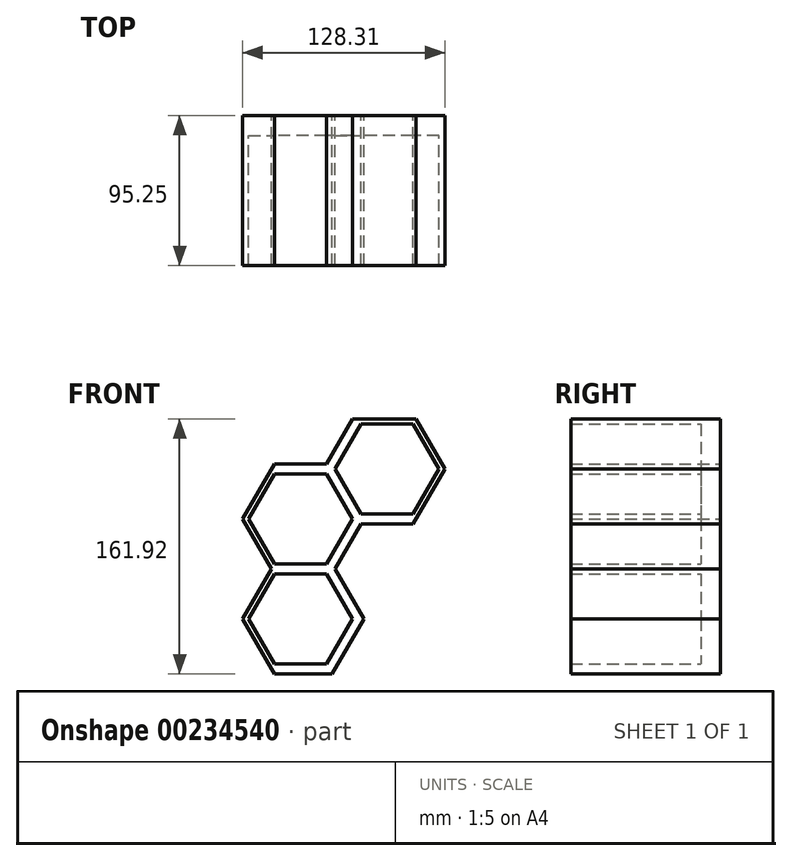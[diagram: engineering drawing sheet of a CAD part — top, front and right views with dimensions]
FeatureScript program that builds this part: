
annotation { "Feature Type Name" : "Feature", "Feature Type Description" : "" }
export const myFeature = defineFeature(function(context is Context, id is Id, definition is map)
    precondition{}
    {
        {
            var Q0;
            Q0=qCreatedBy(makeId("Front.planeOp"),FACE);
            var sketch = newSketch(context, id + "F0", { "sketchPlane" : qUnion([Q0])});
            skLineSegment(sketch, "E0.1", {"start": v(-4.28, 35.04) * mm, "end": v(27.5, 35.04) * mm});
            skCircle(sketch, "E1.cCircle", {"center": v(-40.94, 35.04) * mm, "radius": 28.58 * mm, "construction": true});
            skLineSegment(sketch, "E1.0", {"start": v(-73.94, 35.04) * mm, "end": v(-57.44, 63.62) * mm});
            skLineSegment(sketch, "E1.1", {"start": v(-57.44, 63.62) * mm, "end": v(-24.44, 63.62) * mm});
            skLineSegment(sketch, "E1.2", {"start": v(-24.44, 63.62) * mm, "end": v(-7.94, 35.04) * mm});
            skLineSegment(sketch, "E1.3", {"start": v(-7.94, 35.04) * mm, "end": v(-24.44, 6.47) * mm});
            skLineSegment(sketch, "E1.4", {"start": v(-24.44, 6.47) * mm, "end": v(-57.44, 6.47) * mm});
            skLineSegment(sketch, "E1.5", {"start": v(-57.44, 6.47) * mm, "end": v(-73.94, 35.04) * mm});
            skPoint(sketch, "E1.0.midPoint", {"position": v(-65.69, 49.33) * mm});
            skCircle(sketch, "E2.cCircle", {"center": v(-40.94, 35.04) * mm, "radius": 31.75 * mm, "construction": true});
            skLineSegment(sketch, "E2.0", {"start": v(-77.6, 35.04) * mm, "end": v(-59.27, 66.8) * mm});
            skLineSegment(sketch, "E2.1", {"start": v(-59.27, 66.8) * mm, "end": v(-22.6, 66.8) * mm});
            skLineSegment(sketch, "E2.2", {"start": v(-22.6, 66.8) * mm, "end": v(-4.28, 35.04) * mm});
            skLineSegment(sketch, "E2.3", {"start": v(-4.28, 35.04) * mm, "end": v(-22.6, 3.3) * mm});
            skLineSegment(sketch, "E2.4", {"start": v(-22.6, 3.3) * mm, "end": v(-59.27, 3.3) * mm});
            skLineSegment(sketch, "E2.5", {"start": v(-59.27, 3.3) * mm, "end": v(-77.6, 35.04) * mm});
            skPoint(sketch, "E2.0.midPoint", {"position": v(-68.44, 50.92) * mm});
            skLineSegment(sketch, "E3.2", {"start": v(-77.6, 35.04) * mm, "end": v(-59.27, 3.3) * mm});
            skLineSegment(sketch, "E3.3", {"start": v(-59.27, 3.3) * mm, "end": v(-77.6, -28.46) * mm});
            skLineSegment(sketch, "E4.3", {"start": v(-59.27, 66.8) * mm, "end": v(-77.6, 35.04) * mm});
            skCircle(sketch, "E5.cCircle", {"center": v(14.05, 66.8) * mm, "radius": 28.58 * mm, "construction": true});
            skLineSegment(sketch, "E5.0", {"start": v(-18.94, 66.8) * mm, "end": v(-2.45, 95.37) * mm});
            skLineSegment(sketch, "E5.1", {"start": v(-2.45, 95.37) * mm, "end": v(30.55, 95.37) * mm});
            skLineSegment(sketch, "E5.2", {"start": v(30.55, 95.37) * mm, "end": v(47.05, 66.8) * mm});
            skLineSegment(sketch, "E5.3", {"start": v(47.05, 66.8) * mm, "end": v(30.55, 38.22) * mm});
            skLineSegment(sketch, "E5.4", {"start": v(30.55, 38.22) * mm, "end": v(-2.45, 38.22) * mm});
            skLineSegment(sketch, "E5.5", {"start": v(-2.45, 38.22) * mm, "end": v(-18.94, 66.8) * mm});
            skPoint(sketch, "E5.0.midPoint", {"position": v(-10.7, 81.08) * mm});
            skCircle(sketch, "E6.cCircle", {"center": v(14.05, 66.8) * mm, "radius": 31.75 * mm, "construction": true});
            skLineSegment(sketch, "E6.0", {"start": v(-22.6, 66.8) * mm, "end": v(-4.28, 98.54) * mm});
            skLineSegment(sketch, "E6.1", {"start": v(-4.28, 98.54) * mm, "end": v(32.38, 98.54) * mm});
            skLineSegment(sketch, "E6.2", {"start": v(32.38, 98.54) * mm, "end": v(50.71, 66.8) * mm});
            skLineSegment(sketch, "E6.3", {"start": v(50.71, 66.8) * mm, "end": v(32.38, 35.04) * mm});
            skLineSegment(sketch, "E6.4", {"start": v(32.38, 35.04) * mm, "end": v(-4.28, 35.04) * mm});
            skLineSegment(sketch, "E6.5", {"start": v(-4.28, 35.04) * mm, "end": v(-22.6, 66.8) * mm});
            skPoint(sketch, "E6.0.midPoint", {"position": v(-13.44, 82.67) * mm});
            skLineSegment(sketch, "E7.4", {"start": v(-27.5, 66.8) * mm, "end": v(-59.27, 66.8) * mm});
            skCircle(sketch, "E8.cCircle", {"center": v(-40.94, -28.46) * mm, "radius": 28.58 * mm, "construction": true});
            skLineSegment(sketch, "E8.0", {"start": v(-73.94, -28.46) * mm, "end": v(-57.44, 0.12) * mm});
            skLineSegment(sketch, "E8.1", {"start": v(-57.44, 0.12) * mm, "end": v(-24.44, 0.12) * mm});
            skLineSegment(sketch, "E8.2", {"start": v(-24.44, 0.12) * mm, "end": v(-7.94, -28.46) * mm});
            skLineSegment(sketch, "E8.3", {"start": v(-7.94, -28.46) * mm, "end": v(-24.44, -57.03) * mm});
            skLineSegment(sketch, "E8.4", {"start": v(-24.44, -57.03) * mm, "end": v(-57.44, -57.03) * mm});
            skLineSegment(sketch, "E8.5", {"start": v(-57.44, -57.03) * mm, "end": v(-73.94, -28.46) * mm});
            skPoint(sketch, "E8.0.midPoint", {"position": v(-65.69, -14.17) * mm});
            skCircle(sketch, "E9.cCircle", {"center": v(-40.94, -28.46) * mm, "radius": 31.75 * mm, "construction": true});
            skLineSegment(sketch, "E9.0", {"start": v(-77.6, -28.46) * mm, "end": v(-59.27, 3.3) * mm});
            skLineSegment(sketch, "E9.1", {"start": v(-59.27, 3.3) * mm, "end": v(-22.6, 3.3) * mm});
            skLineSegment(sketch, "E9.2", {"start": v(-22.6, 3.3) * mm, "end": v(-4.28, -28.46) * mm});
            skLineSegment(sketch, "E9.3", {"start": v(-4.28, -28.46) * mm, "end": v(-22.6, -60.2) * mm});
            skLineSegment(sketch, "E9.4", {"start": v(-22.6, -60.2) * mm, "end": v(-59.27, -60.2) * mm});
            skLineSegment(sketch, "E9.5", {"start": v(-59.27, -60.2) * mm, "end": v(-77.6, -28.46) * mm});
            skPoint(sketch, "E9.0.midPoint", {"position": v(-68.44, -12.58) * mm});
            skLineSegment(sketch, "E10.2", {"start": v(-77.6, -28.46) * mm, "end": v(-59.27, -60.2) * mm});
            skLineSegment(sketch, "E11.4", {"start": v(32.38, 98.54) * mm, "end": v(-4.28, 98.54) * mm});
            skLineSegment(sketch, "E12.5", {"start": v(50.71, 66.8) * mm, "end": v(32.38, 98.54) * mm});
            skLineSegment(sketch, "E13.0", {"start": v(32.38, 35.04) * mm, "end": v(50.71, 66.8) * mm});
            skPoint(sketch, "E13.0.midPoint", {"position": v(41.55, 50.92) * mm});
            skLineSegment(sketch, "E14", {"start": v(-57.44, -63.38) * mm, "end": v(-20.78, -63.38) * mm});
            skLineSegment(sketch, "E15", {"start": v(-20.78, -63.38) * mm, "end": v(-0.61, -28.46) * mm});
            skLineSegment(sketch, "E16", {"start": v(-0.61, -28.46) * mm, "end": v(-18.94, 3.3) * mm});
            skLineSegment(sketch, "E17", {"start": v(-18.94, 3.3) * mm, "end": v(-2.45, 31.87) * mm});
            skLineSegment(sketch, "E18", {"start": v(-2.45, 31.87) * mm, "end": v(30.55, 31.87) * mm});
            skLineSegment(sketch, "E19", {"start": v(-57.44, 69.97) * mm, "end": v(-24.44, 69.97) * mm});
            skLineSegment(sketch, "E20", {"start": v(-24.44, 69.97) * mm, "end": v(-7.94, 98.54) * mm});
            skLineSegment(sketch, "E21", {"start": v(-7.94, 98.54) * mm, "end": v(-4.28, 98.54) * mm});
            skLineSegment(sketch, "E22", {"start": v(-57.44, 69.97) * mm, "end": v(-59.27, 66.8) * mm});
            skLineSegment(sketch, "E23", {"start": v(-59.27, -60.2) * mm, "end": v(-57.44, -63.38) * mm});
            skLineSegment(sketch, "E24", {"start": v(30.55, 31.87) * mm, "end": v(32.38, 35.04) * mm});
            skSolve(sketch);
        }
        {
            var Q0;
            Q0=makeQuery(id+"F0.imprint","IMPRINT",FACE,{"disambiguationData":[TD([[makeQuery(id+"F0.imprint","IMPRINT",EDGE,{"derivedFrom":sQuery(id+"F0.wireOp",EDGE,"68d16a58-0471-4e1c-b2b3-2a61df7c0d9d.0")}),-1.0]])]});
            var Q1;
            Q1=makeQuery(id+"F0.imprint","IMPRINT",FACE,{"disambiguationData":[TD([[makeQuery(id+"F0.imprint","IMPRINT",EDGE,{"derivedFrom":sQuery(id+"F0.wireOp",EDGE,"ae29455d-c252-400a-b569-c5a1c48e1351.0")}),-1.0]])]});
            var Q2;
            Q2=makeQuery(id+"F0.imprint","IMPRINT",FACE,{"disambiguationData":[TD([[makeQuery(id+"F0.imprint","IMPRINT",EDGE,{"derivedFrom":sQuery(id+"F0.wireOp",EDGE,"cad1e4f3-bd43-45ec-b31a-1d5006939c94.0")}),-1.0]])]});
            var Q3;
            Q3=makeQuery(id+"F0.imprint","IMPRINT",FACE,{"disambiguationData":[TD([[makeQuery(id+"F0.imprint","IMPRINT",EDGE,{"derivedFrom":sQuery(id+"F0.wireOp",EDGE,"b43d4d8c-f78a-4ff8-8565-99a66ce6ec5f.0")}),-1.0]])]});
            var Q4;
            Q4=makeQuery(id+"F0.imprint","IMPRINT",FACE,{"disambiguationData":[TD([[makeQuery(id+"F0.imprint","IMPRINT",EDGE,{"derivedFrom":sQuery(id+"F0.wireOp",EDGE,"8c75d941-d110-4871-aa41-90a72d60fb2b.0")}),-1.0]])]});
            var Q5;
            Q5=makeQuery(id+"F0.imprint","IMPRINT",FACE,{"disambiguationData":[TD([[makeQuery(id+"F0.imprint","IMPRINT",EDGE,{"derivedFrom":sQuery(id+"F0.wireOp",EDGE,"258573fa-3544-418e-8bc5-5d37e5b8ba09.0")}),-1.0]])]});
            var Q6;
            Q6=makeQuery(id+"F0.imprint","IMPRINT",FACE,{"disambiguationData":[TD([[makeQuery(id+"F0.imprint","IMPRINT",EDGE,{"derivedFrom":sQuery(id+"F0.wireOp",EDGE,"0bf0733b-7d93-4c2e-8366-56d2cde24658.0")}),-1.0]])]});
            var Q7;
            Q7=makeQuery(id+"F0.imprint","IMPRINT",FACE,{"disambiguationData":[TD([[makeQuery(id+"F0.imprint","IMPRINT",EDGE,{"derivedFrom":sQuery(id+"F0.wireOp",EDGE,"E5.0")}),-1.0]])]});
            var Q8;
            Q8=makeQuery(id+"F0.imprint","IMPRINT",FACE,{"disambiguationData":[TD([[makeQuery(id+"F0.imprint","IMPRINT",EDGE,{"derivedFrom":sQuery(id+"F0.wireOp",EDGE,"f16ea8c9-6b67-4651-8441-f7eb3c0ce7d7.0")}),-1.0]])]});
            var Q9;
            Q9=makeQuery(id+"F0.imprint","IMPRINT",FACE,{"disambiguationData":[TD([[makeQuery(id+"F0.imprint","IMPRINT",EDGE,{"derivedFrom":sQuery(id+"F0.wireOp",EDGE,"0306a0a6-7289-4661-a415-5fa5585f2cb5.0")}),-1.0]])]});
            var Q10;
            Q10=makeQuery(id+"F0.imprint","IMPRINT",FACE,{"disambiguationData":[TD([[makeQuery(id+"F0.imprint","IMPRINT",EDGE,{"derivedFrom":sQuery(id+"F0.wireOp",EDGE,"E8.0")}),-1.0]])]});
            var Q11;
            Q11=makeQuery(id+"F0.imprint","IMPRINT",FACE,{"disambiguationData":[TD([[makeQuery(id+"F0.imprint","IMPRINT",EDGE,{"derivedFrom":sQuery(id+"F0.wireOp",EDGE,"cbfd9497-f7fe-4f18-9288-d90aa8075d81.0")}),-1.0]])]});
            var Q12;
            Q12=makeQuery(id+"F0.imprint","IMPRINT",FACE,{"disambiguationData":[TD([[makeQuery(id+"F0.imprint","IMPRINT",EDGE,{"derivedFrom":sQuery(id+"F0.wireOp",EDGE,"6282d196-dd8f-4bb0-bca4-b9108e277473.0")}),-1.0]])]});
            var Q13;
            Q13=makeQuery(id+"F0.imprint","IMPRINT",FACE,{"disambiguationData":[TD([[makeQuery(id+"F0.imprint","IMPRINT",EDGE,{"derivedFrom":sQuery(id+"F0.wireOp",EDGE,"084ca30c-4dc0-463f-bfd9-557787ed9a2f.0")}),-1.0]])]});
            var Q14;
            Q14=makeQuery(id+"F0.imprint","IMPRINT",FACE,{"disambiguationData":[TD([[makeQuery(id+"F0.imprint","IMPRINT",EDGE,{"derivedFrom":sQuery(id+"F0.wireOp",EDGE,"06c29831-6b25-410b-9247-4ee044b7735c.0")}),-1.0]])]});
            var Q15;
            Q15=makeQuery(id+"F0.imprint","IMPRINT",FACE,{"disambiguationData":[TD([[makeQuery(id+"F0.imprint","IMPRINT",EDGE,{"derivedFrom":sQuery(id+"F0.wireOp",EDGE,"b8eec94e-d97e-439b-aaac-63499233db4c.0")}),-1.0]])]});
            var Q16;
            Q16=makeQuery(id+"F0.imprint","IMPRINT",FACE,{"disambiguationData":[TD([[makeQuery(id+"F0.imprint","IMPRINT",EDGE,{"derivedFrom":sQuery(id+"F0.wireOp",EDGE,"2e929887-9bb9-4083-9cef-f9a6a24e8e46.0")}),-1.0]])]});
            var Q17;
            Q17=makeQuery(id+"F0.imprint","IMPRINT",FACE,{"disambiguationData":[TD([[makeQuery(id+"F0.imprint","IMPRINT",EDGE,{"derivedFrom":sQuery(id+"F0.wireOp",EDGE,"23671680-92ab-419e-a071-eb0943a5012b.0")}),-1.0]])]});
            var Q18;
            Q18=makeQuery(id+"F0.imprint","IMPRINT",FACE,{"disambiguationData":[TD([[makeQuery(id+"F0.imprint","IMPRINT",EDGE,{"derivedFrom":sQuery(id+"F0.wireOp",EDGE,"E1.0")}),-1.0]])]});
            var Q19;
            Q19=makeQuery(id+"F0.imprint","IMPRINT",FACE,{"disambiguationData":[TD([[makeQuery(id+"F0.imprint","IMPRINT",EDGE,{"derivedFrom":sQuery(id+"F0.wireOp",EDGE,"37efd634-c264-4683-8864-08b38c7986ca.0")}),-1.0]])]});
            var Q20;
            Q20=makeQuery(id+"F0.imprint","IMPRINT",FACE,{"disambiguationData":[TD([[makeQuery(id+"F0.imprint","IMPRINT",EDGE,{"derivedFrom":sQuery(id+"F0.wireOp",EDGE,"f2dd3995-374a-43c5-8725-4a87181dc8c5.0")}),-1.0]])]});
            var Q21;
            Q21=makeQuery(id+"F0.imprint","IMPRINT",FACE,{"disambiguationData":[TD([[makeQuery(id+"F0.imprint","IMPRINT",EDGE,{"derivedFrom":sQuery(id+"F0.wireOp",EDGE,"1f2aec04-a318-49b9-a42e-ea2fce35ed6c.0")}),-1.0]])]});
            var Q22;
            Q22=makeQuery(id+"F0.imprint","IMPRINT",FACE,{"disambiguationData":[TD([[makeQuery(id+"F0.imprint","IMPRINT",EDGE,{"derivedFrom":sQuery(id+"F0.wireOp",EDGE,"f97fdbdd-69fc-44f1-b8f7-f6a6a25558e6.0")}),-1.0]])]});
            var Q23;
            Q23=makeQuery(id+"F0.imprint","IMPRINT",FACE,{"disambiguationData":[TD([[makeQuery(id+"F0.imprint","IMPRINT",EDGE,{"derivedFrom":sQuery(id+"F0.wireOp",EDGE,"4e92e904-9607-490d-a429-b319c41500d9.0")}),-1.0]])]});
            var Q24;
            Q24=makeQuery(id+"F0.imprint","IMPRINT",FACE,{"disambiguationData":[TD([[makeQuery(id+"F0.imprint","IMPRINT",EDGE,{"derivedFrom":sQuery(id+"F0.wireOp",EDGE,"084ca30c-4dc0-463f-bfd9-557787ed9a2f.0")}),1.0]])]});
            var Q25;
            Q25=makeQuery(id+"F0.imprint","IMPRINT",FACE,{"disambiguationData":[TD([[makeQuery(id+"F0.imprint","IMPRINT",EDGE,{"derivedFrom":sQuery(id+"F0.wireOp",EDGE,"1f2aec04-a318-49b9-a42e-ea2fce35ed6c.0")}),1.0]])]});
            var Q26;
            Q26=makeQuery(id+"F0.imprint","IMPRINT",FACE,{"disambiguationData":[TD([[makeQuery(id+"F0.imprint","IMPRINT",EDGE,{"derivedFrom":sQuery(id+"F0.wireOp",EDGE,"23671680-92ab-419e-a071-eb0943a5012b.0")}),1.0]])]});
            var Q27;
            Q27=makeQuery(id+"F0.imprint","IMPRINT",FACE,{"disambiguationData":[TD([[makeQuery(id+"F0.imprint","IMPRINT",EDGE,{"derivedFrom":sQuery(id+"F0.wireOp",EDGE,"2e929887-9bb9-4083-9cef-f9a6a24e8e46.0")}),1.0]])]});
            var Q28;
            Q28=makeQuery(id+"F0.imprint","IMPRINT",FACE,{"disambiguationData":[TD([[makeQuery(id+"F0.imprint","IMPRINT",EDGE,{"derivedFrom":sQuery(id+"F0.wireOp",EDGE,"4e92e904-9607-490d-a429-b319c41500d9.0")}),1.0]])]});
            var Q29;
            Q29=makeQuery(id+"F0.imprint","IMPRINT",FACE,{"disambiguationData":[TD([[makeQuery(id+"F0.imprint","IMPRINT",EDGE,{"derivedFrom":sQuery(id+"F0.wireOp",EDGE,"b43d4d8c-f78a-4ff8-8565-99a66ce6ec5f.0")}),1.0]])]});
            var Q30;
            Q30=makeQuery(id+"F0.imprint","IMPRINT",FACE,{"disambiguationData":[TD([[makeQuery(id+"F0.imprint","IMPRINT",EDGE,{"derivedFrom":sQuery(id+"F0.wireOp",EDGE,"ae29455d-c252-400a-b569-c5a1c48e1351.0")}),1.0]])]});
            var Q31;
            Q31=makeQuery(id+"F0.imprint","IMPRINT",FACE,{"disambiguationData":[TD([[makeQuery(id+"F0.imprint","IMPRINT",EDGE,{"derivedFrom":sQuery(id+"F0.wireOp",EDGE,"E8.0")}),1.0]])]});
            var Q32;
            Q32=makeQuery(id+"F0.imprint","IMPRINT",FACE,{"disambiguationData":[TD([[makeQuery(id+"F0.imprint","IMPRINT",EDGE,{"derivedFrom":sQuery(id+"F0.wireOp",EDGE,"258573fa-3544-418e-8bc5-5d37e5b8ba09.0")}),1.0]])]});
            var Q33;
            Q33=makeQuery(id+"F0.imprint","IMPRINT",FACE,{"disambiguationData":[TD([[makeQuery(id+"F0.imprint","IMPRINT",EDGE,{"derivedFrom":sQuery(id+"F0.wireOp",EDGE,"cbfd9497-f7fe-4f18-9288-d90aa8075d81.0")}),1.0]])]});
            var Q34;
            Q34=makeQuery(id+"F0.imprint","IMPRINT",FACE,{"disambiguationData":[TD([[makeQuery(id+"F0.imprint","IMPRINT",EDGE,{"derivedFrom":sQuery(id+"F0.wireOp",EDGE,"f97fdbdd-69fc-44f1-b8f7-f6a6a25558e6.0")}),1.0]])]});
            var Q35;
            Q35=makeQuery(id+"F0.imprint","IMPRINT",FACE,{"disambiguationData":[TD([[makeQuery(id+"F0.imprint","IMPRINT",EDGE,{"derivedFrom":sQuery(id+"F0.wireOp",EDGE,"b8eec94e-d97e-439b-aaac-63499233db4c.0")}),1.0]])]});
            var Q36;
            Q36=makeQuery(id+"F0.imprint","IMPRINT",FACE,{"disambiguationData":[TD([[makeQuery(id+"F0.imprint","IMPRINT",EDGE,{"derivedFrom":sQuery(id+"F0.wireOp",EDGE,"8c75d941-d110-4871-aa41-90a72d60fb2b.0")}),1.0]])]});
            var Q37;
            Q37=makeQuery(id+"F0.imprint","IMPRINT",FACE,{"disambiguationData":[TD([[makeQuery(id+"F0.imprint","IMPRINT",EDGE,{"derivedFrom":sQuery(id+"F0.wireOp",EDGE,"f16ea8c9-6b67-4651-8441-f7eb3c0ce7d7.0")}),1.0]])]});
            var Q38;
            Q38=makeQuery(id+"F0.imprint","IMPRINT",FACE,{"disambiguationData":[TD([[makeQuery(id+"F0.imprint","IMPRINT",EDGE,{"derivedFrom":sQuery(id+"F0.wireOp",EDGE,"37efd634-c264-4683-8864-08b38c7986ca.0")}),1.0]])]});
            var Q39;
            Q39=makeQuery(id+"F0.imprint","IMPRINT",FACE,{"disambiguationData":[TD([[makeQuery(id+"F0.imprint","IMPRINT",EDGE,{"derivedFrom":sQuery(id+"F0.wireOp",EDGE,"68d16a58-0471-4e1c-b2b3-2a61df7c0d9d.0")}),1.0]])]});
            var Q40;
            Q40=makeQuery(id+"F0.imprint","IMPRINT",FACE,{"disambiguationData":[TD([[makeQuery(id+"F0.imprint","IMPRINT",EDGE,{"derivedFrom":sQuery(id+"F0.wireOp",EDGE,"0306a0a6-7289-4661-a415-5fa5585f2cb5.0")}),1.0]])]});
            var Q41;
            Q41=makeQuery(id+"F0.imprint","IMPRINT",FACE,{"disambiguationData":[TD([[makeQuery(id+"F0.imprint","IMPRINT",EDGE,{"derivedFrom":sQuery(id+"F0.wireOp",EDGE,"0bf0733b-7d93-4c2e-8366-56d2cde24658.0")}),1.0]])]});
            var Q42;
            Q42=makeQuery(id+"F0.imprint","IMPRINT",FACE,{"disambiguationData":[TD([[makeQuery(id+"F0.imprint","IMPRINT",EDGE,{"derivedFrom":sQuery(id+"F0.wireOp",EDGE,"06c29831-6b25-410b-9247-4ee044b7735c.0")}),1.0]])]});
            var Q43;
            Q43=makeQuery(id+"F0.imprint","IMPRINT",FACE,{"disambiguationData":[TD([[makeQuery(id+"F0.imprint","IMPRINT",EDGE,{"derivedFrom":sQuery(id+"F0.wireOp",EDGE,"6282d196-dd8f-4bb0-bca4-b9108e277473.0")}),1.0]])]});
            var Q44;
            Q44=makeQuery(id+"F0.imprint","IMPRINT",FACE,{"disambiguationData":[TD([[makeQuery(id+"F0.imprint","IMPRINT",EDGE,{"derivedFrom":sQuery(id+"F0.wireOp",EDGE,"cad1e4f3-bd43-45ec-b31a-1d5006939c94.0")}),1.0]])]});
            var Q45;
            Q45=makeQuery(id+"F0.imprint","IMPRINT",FACE,{"disambiguationData":[TD([[makeQuery(id+"F0.imprint","IMPRINT",EDGE,{"derivedFrom":sQuery(id+"F0.wireOp",EDGE,"f2dd3995-374a-43c5-8725-4a87181dc8c5.0")}),1.0]])]});
            var Q46;
            Q46=makeQuery(id+"F0.imprint","IMPRINT",FACE,{"disambiguationData":[TD([[makeQuery(id+"F0.imprint","IMPRINT",EDGE,{"derivedFrom":sQuery(id+"F0.wireOp",EDGE,"E1.0")}),1.0]])]});
            var Q47;
            Q47=makeQuery(id+"F0.imprint","IMPRINT",FACE,{"disambiguationData":[TD([[makeQuery(id+"F0.imprint","IMPRINT",EDGE,{"derivedFrom":sQuery(id+"F0.wireOp",EDGE,"E5.0")}),1.0]])]});
            extrude(context, id + "F1", {"entities" : qUnion([Q0, Q1, Q2, Q3, Q4, Q5, Q6, Q7, Q8, Q9, Q10, Q11, Q12, Q13, Q14, Q15, Q16, Q17, Q18, Q19, Q20, Q21, Q22, Q23, Q24, Q25, Q26, Q27, Q28, Q29, Q30, Q31, Q32, Q33, Q34, Q35, Q36, Q37, Q38, Q39, Q40, Q41, Q42, Q43, Q44, Q45, Q46, Q47]), "depth" : 12.7 * mm});
        }
        {
            var Q0;
            Q0=makeQuery(id+"F0.imprint","IMPRINT",FACE,{"disambiguationData":[TD([[makeQuery(id+"F0.imprint","IMPRINT",EDGE,{"derivedFrom":sQuery(id+"F0.wireOp",EDGE,"8c75d941-d110-4871-aa41-90a72d60fb2b.0")}),1.0]])]});
            var Q1;
            Q1=makeQuery(id+"F0.imprint","IMPRINT",FACE,{"disambiguationData":[TD([[makeQuery(id+"F0.imprint","IMPRINT",EDGE,{"derivedFrom":sQuery(id+"F0.wireOp",EDGE,"b8eec94e-d97e-439b-aaac-63499233db4c.0")}),1.0]])]});
            var Q2;
            Q2=makeQuery(id+"F0.imprint","IMPRINT",FACE,{"disambiguationData":[TD([[makeQuery(id+"F0.imprint","IMPRINT",EDGE,{"derivedFrom":sQuery(id+"F0.wireOp",EDGE,"cad1e4f3-bd43-45ec-b31a-1d5006939c94.0")}),1.0]])]});
            var Q3;
            Q3=makeQuery(id+"F0.imprint","IMPRINT",FACE,{"disambiguationData":[TD([[makeQuery(id+"F0.imprint","IMPRINT",EDGE,{"derivedFrom":sQuery(id+"F0.wireOp",EDGE,"68d16a58-0471-4e1c-b2b3-2a61df7c0d9d.0")}),1.0]])]});
            var Q4;
            Q4=makeQuery(id+"F0.imprint","IMPRINT",FACE,{"disambiguationData":[TD([[makeQuery(id+"F0.imprint","IMPRINT",EDGE,{"derivedFrom":sQuery(id+"F0.wireOp",EDGE,"0306a0a6-7289-4661-a415-5fa5585f2cb5.0")}),1.0]])]});
            var Q5;
            Q5=makeQuery(id+"F0.imprint","IMPRINT",FACE,{"disambiguationData":[TD([[makeQuery(id+"F0.imprint","IMPRINT",EDGE,{"derivedFrom":sQuery(id+"F0.wireOp",EDGE,"084ca30c-4dc0-463f-bfd9-557787ed9a2f.0")}),1.0]])]});
            var Q6;
            Q6=makeQuery(id+"F0.imprint","IMPRINT",FACE,{"disambiguationData":[TD([[makeQuery(id+"F0.imprint","IMPRINT",EDGE,{"derivedFrom":sQuery(id+"F0.wireOp",EDGE,"4e92e904-9607-490d-a429-b319c41500d9.0")}),1.0]])]});
            var Q7;
            Q7=makeQuery(id+"F0.imprint","IMPRINT",FACE,{"disambiguationData":[TD([[makeQuery(id+"F0.imprint","IMPRINT",EDGE,{"derivedFrom":sQuery(id+"F0.wireOp",EDGE,"E1.0")}),1.0]])]});
            var Q8;
            Q8=makeQuery(id+"F0.imprint","IMPRINT",FACE,{"disambiguationData":[TD([[makeQuery(id+"F0.imprint","IMPRINT",EDGE,{"derivedFrom":sQuery(id+"F0.wireOp",EDGE,"E5.0")}),1.0]])]});
            var Q9;
            Q9=makeQuery(id+"F0.imprint","IMPRINT",FACE,{"disambiguationData":[TD([[makeQuery(id+"F0.imprint","IMPRINT",EDGE,{"derivedFrom":sQuery(id+"F0.wireOp",EDGE,"258573fa-3544-418e-8bc5-5d37e5b8ba09.0")}),1.0]])]});
            var Q10;
            Q10=makeQuery(id+"F0.imprint","IMPRINT",FACE,{"disambiguationData":[TD([[makeQuery(id+"F0.imprint","IMPRINT",EDGE,{"derivedFrom":sQuery(id+"F0.wireOp",EDGE,"f2dd3995-374a-43c5-8725-4a87181dc8c5.0")}),1.0]])]});
            var Q11;
            Q11=makeQuery(id+"F0.imprint","IMPRINT",FACE,{"disambiguationData":[TD([[makeQuery(id+"F0.imprint","IMPRINT",EDGE,{"derivedFrom":sQuery(id+"F0.wireOp",EDGE,"23671680-92ab-419e-a071-eb0943a5012b.0")}),1.0]])]});
            var Q12;
            Q12=makeQuery(id+"F0.imprint","IMPRINT",FACE,{"disambiguationData":[TD([[makeQuery(id+"F0.imprint","IMPRINT",EDGE,{"derivedFrom":sQuery(id+"F0.wireOp",EDGE,"06c29831-6b25-410b-9247-4ee044b7735c.0")}),1.0]])]});
            var Q13;
            Q13=makeQuery(id+"F0.imprint","IMPRINT",FACE,{"disambiguationData":[TD([[makeQuery(id+"F0.imprint","IMPRINT",EDGE,{"derivedFrom":sQuery(id+"F0.wireOp",EDGE,"ae29455d-c252-400a-b569-c5a1c48e1351.0")}),1.0]])]});
            var Q14;
            Q14=makeQuery(id+"F0.imprint","IMPRINT",FACE,{"disambiguationData":[TD([[makeQuery(id+"F0.imprint","IMPRINT",EDGE,{"derivedFrom":sQuery(id+"F0.wireOp",EDGE,"f97fdbdd-69fc-44f1-b8f7-f6a6a25558e6.0")}),1.0]])]});
            var Q15;
            Q15=makeQuery(id+"F0.imprint","IMPRINT",FACE,{"disambiguationData":[TD([[makeQuery(id+"F0.imprint","IMPRINT",EDGE,{"derivedFrom":sQuery(id+"F0.wireOp",EDGE,"2e929887-9bb9-4083-9cef-f9a6a24e8e46.0")}),1.0]])]});
            var Q16;
            Q16=makeQuery(id+"F0.imprint","IMPRINT",FACE,{"disambiguationData":[TD([[makeQuery(id+"F0.imprint","IMPRINT",EDGE,{"derivedFrom":sQuery(id+"F0.wireOp",EDGE,"E8.0")}),1.0]])]});
            var Q17;
            Q17=makeQuery(id+"F0.imprint","IMPRINT",FACE,{"disambiguationData":[TD([[makeQuery(id+"F0.imprint","IMPRINT",EDGE,{"derivedFrom":sQuery(id+"F0.wireOp",EDGE,"37efd634-c264-4683-8864-08b38c7986ca.0")}),1.0]])]});
            var Q18;
            Q18=makeQuery(id+"F0.imprint","IMPRINT",FACE,{"disambiguationData":[TD([[makeQuery(id+"F0.imprint","IMPRINT",EDGE,{"derivedFrom":sQuery(id+"F0.wireOp",EDGE,"cbfd9497-f7fe-4f18-9288-d90aa8075d81.0")}),1.0]])]});
            var Q19;
            Q19=makeQuery(id+"F0.imprint","IMPRINT",FACE,{"disambiguationData":[TD([[makeQuery(id+"F0.imprint","IMPRINT",EDGE,{"derivedFrom":sQuery(id+"F0.wireOp",EDGE,"6282d196-dd8f-4bb0-bca4-b9108e277473.0")}),1.0]])]});
            var Q20;
            Q20=makeQuery(id+"F0.imprint","IMPRINT",FACE,{"disambiguationData":[TD([[makeQuery(id+"F0.imprint","IMPRINT",EDGE,{"derivedFrom":sQuery(id+"F0.wireOp",EDGE,"0bf0733b-7d93-4c2e-8366-56d2cde24658.0")}),1.0]])]});
            var Q21;
            Q21=makeQuery(id+"F0.imprint","IMPRINT",FACE,{"disambiguationData":[TD([[makeQuery(id+"F0.imprint","IMPRINT",EDGE,{"derivedFrom":sQuery(id+"F0.wireOp",EDGE,"b43d4d8c-f78a-4ff8-8565-99a66ce6ec5f.0")}),1.0]])]});
            var Q22;
            Q22=makeQuery(id+"F0.imprint","IMPRINT",FACE,{"disambiguationData":[TD([[makeQuery(id+"F0.imprint","IMPRINT",EDGE,{"derivedFrom":sQuery(id+"F0.wireOp",EDGE,"f16ea8c9-6b67-4651-8441-f7eb3c0ce7d7.0")}),1.0]])]});
            var Q23;
            Q23=makeQuery(id+"F0.imprint","IMPRINT",FACE,{"disambiguationData":[TD([[makeQuery(id+"F0.imprint","IMPRINT",EDGE,{"derivedFrom":sQuery(id+"F0.wireOp",EDGE,"1f2aec04-a318-49b9-a42e-ea2fce35ed6c.0")}),1.0]])]});
            var Q24;
            {var subQ6=sQuery(id+"F0.wireOp",EDGE,"E2.3");Q24=makeQuery(id+"F0.imprint","IMPRINT",FACE,{"disambiguationData":[TD([[makeQuery(id+"F0.imprint","IMPRINT",EDGE,{"derivedFrom":subQ6}),1.0]])]});}
            var Q25;
            Q25=makeQuery(id+"F0.imprint","IMPRINT",FACE,{"disambiguationData":[TD([[makeQuery(id+"F0.imprint","IMPRINT",EDGE,{"derivedFrom":sQuery(id+"F0.wireOp",EDGE,"E2.1")}),1.0]])]});
            extrude(context, id + "F2", {"entities" : qUnion([Q0, Q1, Q2, Q3, Q4, Q5, Q6, Q7, Q8, Q9, Q10, Q11, Q12, Q13, Q14, Q15, Q16, Q17, Q18, Q19, Q20, Q21, Q22, Q23, Q24, Q25]), "operationType" : NewBodyOperationType.ADD, "depth" : 95.25 * mm});
        }
    });
